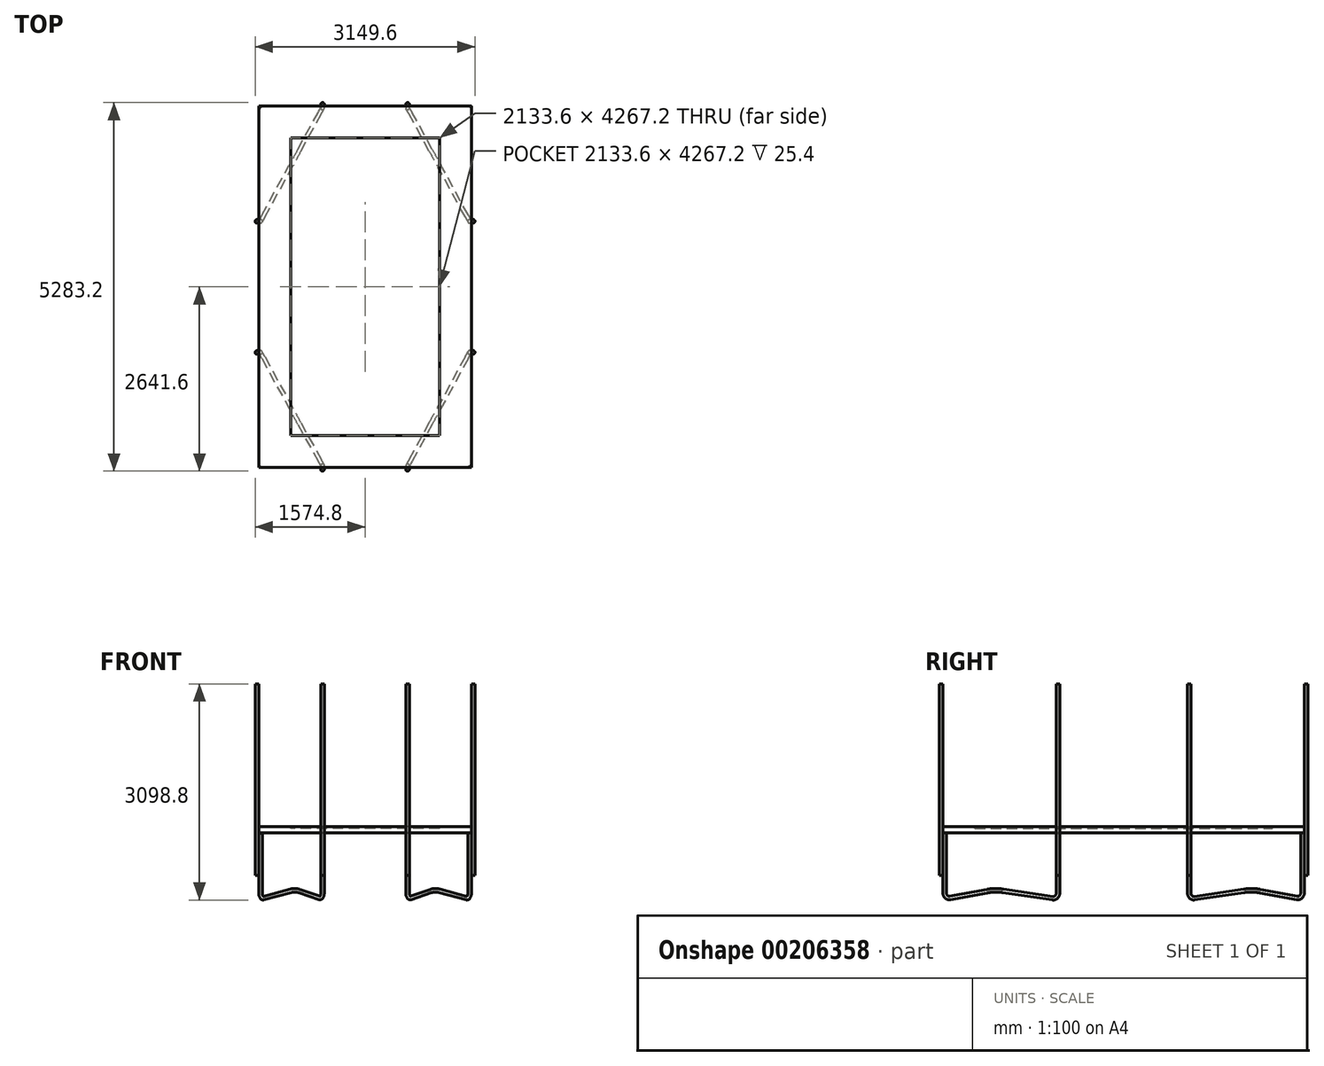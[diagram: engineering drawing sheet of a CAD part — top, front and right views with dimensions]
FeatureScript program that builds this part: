
annotation { "Feature Type Name" : "Feature", "Feature Type Description" : "" }
export const myFeature = defineFeature(function(context is Context, id is Id, definition is map)
    precondition{}
    {
        {
            var Q0;
            Q0=qCreatedBy(makeId("Top.planeOp"),FACE);
            var sketch = newSketch(context, id + "F0", { "sketchPlane" : qUnion([Q0])});
            skLineSegment(sketch, "E0.bottom", {"start": v(1524, -2590.8) * mm, "end": v(-1524, -2590.8) * mm});
            skLineSegment(sketch, "E0.top", {"start": v(1524, 2590.8) * mm, "end": v(-1524, 2590.8) * mm});
            skLineSegment(sketch, "E0.left", {"start": v(1524, -2590.8) * mm, "end": v(1524, 2590.8) * mm});
            skLineSegment(sketch, "E0.right", {"start": v(-1524, -2590.8) * mm, "end": v(-1524, 2590.8) * mm});
            skPoint(sketch, "E0.middle", {"position": v(0, 0) * mm});
            skSolve(sketch);
        }
        {
            var Q0;
            Q0 = qSketchRegion(id + "F0", true);
            extrude(context, id + "F1", {"entities" : qUnion([Q0]), "depth" : 88.9 * mm});
        }
        {
            var Q0;
            Q0=makeQuery(id+"F1.opExtrude","CAP_EDGE",EDGE,{"disambiguationData":[OSD([sQuery(id+"F0.wireOp",EDGE,"E0.right")])],"isStart":false});
            var Q1;
            Q1=makeQuery(id+"F1.opExtrude","CAP_EDGE",EDGE,{"disambiguationData":[OSD([sQuery(id+"F0.wireOp",EDGE,"E0.bottom")])],"isStart":false});
            var Q2;
            Q2=makeQuery(id+"F1.opExtrude","CAP_EDGE",EDGE,{"disambiguationData":[OSD([sQuery(id+"F0.wireOp",EDGE,"E0.left")])],"isStart":false});
            var Q3;
            Q3=makeQuery(id+"F1.opExtrude","CAP_EDGE",EDGE,{"disambiguationData":[OSD([sQuery(id+"F0.wireOp",EDGE,"E0.top")])],"isStart":false});
            fillet(context, id + "F2", {"entities" : qUnion([Q0, Q1, Q2, Q3]), "radius" : 25.4 * mm, "tangentPropagation" : true, "allowEdgeOverflow" : false});
        }
        {
            var Q0;
            Q0=makeQuery(id+"F1.opExtrude","CAP_FACE",FACE,{"disambiguationData":[OSD([sQuery(id+"F0.wireOp",EDGE,"E0.bottom"),sQuery(id+"F0.wireOp",EDGE,"E0.top"),sQuery(id+"F0.wireOp",EDGE,"E0.left"),sQuery(id+"F0.wireOp",EDGE,"E0.right")])],"isStart":false});
            var sketch = newSketch(context, id + "F3", { "sketchPlane" : qUnion([Q0])});
            skLineSegment(sketch, "E1.bottom", {"start": v(1066.8, -2133.6) * mm, "end": v(-1066.8, -2133.6) * mm});
            skLineSegment(sketch, "E1.top", {"start": v(1066.8, 2133.6) * mm, "end": v(-1066.8, 2133.6) * mm});
            skLineSegment(sketch, "E1.left", {"start": v(1066.8, -2133.6) * mm, "end": v(1066.8, 2133.6) * mm});
            skLineSegment(sketch, "E1.right", {"start": v(-1066.8, -2133.6) * mm, "end": v(-1066.8, 2133.6) * mm});
            skPoint(sketch, "E1.middle", {"position": v(0, 0) * mm});
            skSolve(sketch);
        }
        {
            var Q0;
            Q0 = qSketchRegion(id + "F3", true);
            extrude(context, id + "F4", {"entities" : qUnion([Q0]), "operationType" : NewBodyOperationType.REMOVE, "oppositeDirection" : true, "depth" : 25.4 * mm});
        }
        {
            var Q0;
            Q0=makeQuery(id+"F1.opExtrude","CAP_FACE",FACE,{"disambiguationData":[OSD([sQuery(id+"F0.wireOp",EDGE,"E0.bottom"),sQuery(id+"F0.wireOp",EDGE,"E0.top"),sQuery(id+"F0.wireOp",EDGE,"E0.left"),sQuery(id+"F0.wireOp",EDGE,"E0.right")])],"isStart":true});
            var sketch = newSketch(context, id + "F5", { "sketchPlane" : qUnion([Q0])});
            skLineSegment(sketch, "E2", {"start": v(-609.6, 2590.8) * mm, "end": v(-609.6, 2565.4) * mm, "construction": true});
            skLineSegment(sketch, "E3", {"start": v(-609.6, 2565.4) * mm, "end": v(-1498.6, 939.8) * mm, "construction": true});
            skLineSegment(sketch, "E4", {"start": v(-1498.6, 939.8) * mm, "end": v(-1524, 939.8) * mm, "construction": true});
            skCircle(sketch, "E5", {"center": v(-1498.6, 939.8) * mm, "radius": 25.4 * mm});
            skSolve(sketch);
        }
        {
            var Q0;
            Q0=sQuery(id+"F5.wireOp",EDGE,"E3");
            cPlane(context, id + "F6", {"entities" : qUnion([Q0]), "cplaneType" : CPlaneType.LINE_ANGLE, "offset" : 25.4 * mm, "angle" : 90 * degree, "width" : 152.4 * mm, "height" : 152.4 * mm});
        }
        {
            var Q0;
            Q0=qCreatedBy(id+"F6.planeOp",FACE);
            var sketch = newSketch(context, id + "F7", { "sketchPlane" : qUnion([Q0])});
            skLineSegment(sketch, "E6", {"start": v(-105.5, 0) * mm, "end": v(-105.5, -863.6) * mm});
            skLineSegment(sketch, "E7", {"start": v(-191.53, -939.16) * mm, "end": v(-1002.65, -833.74) * mm});
            skLineSegment(sketch, "E8", {"start": v(-1267.29, -837.96) * mm, "end": v(-1869.88, -935.96) * mm});
            skLineSegment(sketch, "E9", {"start": v(-1958.31, -860.75) * mm, "end": v(-1958.31, 0) * mm});
            skPoint(sketch, "E10.visualSharp", {"position": v(-105.5, -950.35) * mm});
            skArc(sketch, "E10.filletArc", {"start": v(-191.53, -939.16) * mm, "mid": v(-131.42, -920.85) * mm, "end": v(-105.5, -863.6) * mm});
            skPoint(sketch, "E11.visualSharp", {"position": v(-1135.28, -816.5) * mm});
            skArc(sketch, "E11.filletArc", {"start": v(-1002.65, -833.74) * mm, "mid": v(-1135.12, -826.22) * mm, "end": v(-1267.29, -837.96) * mm});
            skPoint(sketch, "E12.visualSharp", {"position": v(-1958.31, -950.35) * mm});
            skArc(sketch, "E12.filletArc", {"start": v(-1958.31, -860.75) * mm, "mid": v(-1931.48, -918.8) * mm, "end": v(-1869.88, -935.96) * mm});
            skLineSegment(sketch, "E13", {"start": v(-105.5, -939.8) * mm, "end": v(-1958.31, -939.8) * mm, "construction": true});
            skSolve(sketch);
        }
        {
            var Q0;
            Q0 = qSketchRegion(id + "F5", true);
            extrude(context, id + "F8", {"entities" : qUnion([Q0]), "operationType" : NewBodyOperationType.ADD, "depth" : 6.35 * mm});
        }
        {
            var Q0;
            Q0=makeQuery(id+"F8.opExtrude","CAP_FACE",FACE,{"disambiguationData":[OSD([sQuery(id+"F5.wireOp",EDGE,"E5")])],"isStart":false});
            var Q1;
            Q1=sQuery(id+"F5.wireOp",EDGE,"E5");
            var Q2;
            Q2=sQuery(id+"F7.wireOp",EDGE,"E6");
            var Q3;
            Q3=sQuery(id+"F7.wireOp",EDGE,"E10.filletArc");
            var Q4;
            Q4=sQuery(id+"F7.wireOp",EDGE,"E7");
            var Q5;
            Q5=sQuery(id+"F7.wireOp",EDGE,"E11.filletArc");
            var Q6;
            Q6=sQuery(id+"F7.wireOp",EDGE,"E8");
            var Q7;
            Q7=sQuery(id+"F7.wireOp",EDGE,"E12.filletArc");
            var Q8;
            Q8=sQuery(id+"F7.wireOp",EDGE,"E9");
            sweep(context, id + "F9", {"profiles" : qUnion([Q0]), "surfaceProfiles" : qUnion([Q1]), "path" : qUnion([Q2, Q3, Q4, Q5, Q6, Q7, Q8])});
        }
        {
            var Q0;
            Q0=qCreatedBy(makeId("Top.planeOp"),FACE);
            var sketch = newSketch(context, id + "F10", { "sketchPlane" : qUnion([Q0])});
            skCircle(sketch, "E14", {"center": v(-1549.4, -939.8) * mm, "radius": 25.4 * mm});
            skCircle(sketch, "E15", {"center": v(-609.6, -2616.2) * mm, "radius": 25.4 * mm});
            skSolve(sketch);
        }
        {
            var Q0;
            Q0 = qSketchRegion(id + "F10", true);
            extrude(context, id + "F11", {"entities" : qUnion([Q0]), "depth" : 2133.6 * mm, "hasSecondDirection" : true, "secondDirectionOppositeDirection" : true, "secondDirectionDepth" : 609.6 * mm});
        }
        {
            var Q0;
            Q0=makeQuery(id+"F9.opSweep","SWEPT_BODY",BODY,{"disambiguationData":[OSD([sQuery(id+"F5.wireOp",EDGE,"E5"),sQuery(id+"F7.wireOp",EDGE,"E9")])]});
            var Q1;
            Q1=makeQuery(id+"F11.opExtrude","SWEPT_BODY",BODY,{"disambiguationData":[OSD([sQuery(id+"F10.wireOp",EDGE,"E14")])]});
            var Q2;
            Q2=makeQuery(id+"F11.opExtrude","SWEPT_BODY",BODY,{"disambiguationData":[OSD([sQuery(id+"F10.wireOp",EDGE,"E15")])]});
            var Q3;
            Q3=qCreatedBy(makeId("Right.planeOp"),FACE);
            mirror(context, id + "F12", {"entities" : qUnion([Q0, Q1, Q2]), "mirrorPlane" : qUnion([Q3])});
        }
        {
            var Q0;
            Q0=makeQuery(id+"F12.opPattern","COPY",BODY,{"derivedFrom":makeQuery(id+"F9.opSweep","SWEPT_BODY",BODY,{"disambiguationData":[OSD([sQuery(id+"F5.wireOp",EDGE,"E5"),sQuery(id+"F7.wireOp",EDGE,"E9")])]}),"instanceName":"1"});
            var Q1;
            Q1=makeQuery(id+"F9.opSweep","SWEPT_BODY",BODY,{"disambiguationData":[OSD([sQuery(id+"F5.wireOp",EDGE,"E5"),sQuery(id+"F7.wireOp",EDGE,"E9")])]});
            var Q2;
            Q2=makeQuery(id+"F12.opPattern","COPY",BODY,{"derivedFrom":makeQuery(id+"F11.opExtrude","SWEPT_BODY",BODY,{"disambiguationData":[OSD([sQuery(id+"F10.wireOp",EDGE,"E14")])]}),"instanceName":"1"});
            var Q3;
            Q3=makeQuery(id+"F11.opExtrude","SWEPT_BODY",BODY,{"disambiguationData":[OSD([sQuery(id+"F10.wireOp",EDGE,"E14")])]});
            var Q4;
            Q4=makeQuery(id+"F11.opExtrude","SWEPT_BODY",BODY,{"disambiguationData":[OSD([sQuery(id+"F10.wireOp",EDGE,"E15")])]});
            var Q5;
            Q5=makeQuery(id+"F1.opExtrude","SWEPT_BODY",BODY,{"disambiguationData":[OSD([sQuery(id+"F0.wireOp",EDGE,"E0.bottom"),sQuery(id+"F0.wireOp",EDGE,"E0.top"),sQuery(id+"F0.wireOp",EDGE,"E0.left"),sQuery(id+"F0.wireOp",EDGE,"E0.right")])]});
            var Q6;
            Q6=makeQuery(id+"F12.opPattern","COPY",BODY,{"derivedFrom":makeQuery(id+"F11.opExtrude","SWEPT_BODY",BODY,{"disambiguationData":[OSD([sQuery(id+"F10.wireOp",EDGE,"E15")])]}),"instanceName":"1"});
            var Q7;
            Q7=qCreatedBy(makeId("Front.planeOp"),FACE);
            mirror(context, id + "F13", {"entities" : qUnion([Q0, Q1, Q2, Q3, Q4, Q5, Q6]), "mirrorPlane" : qUnion([Q7])});
        }
    });
